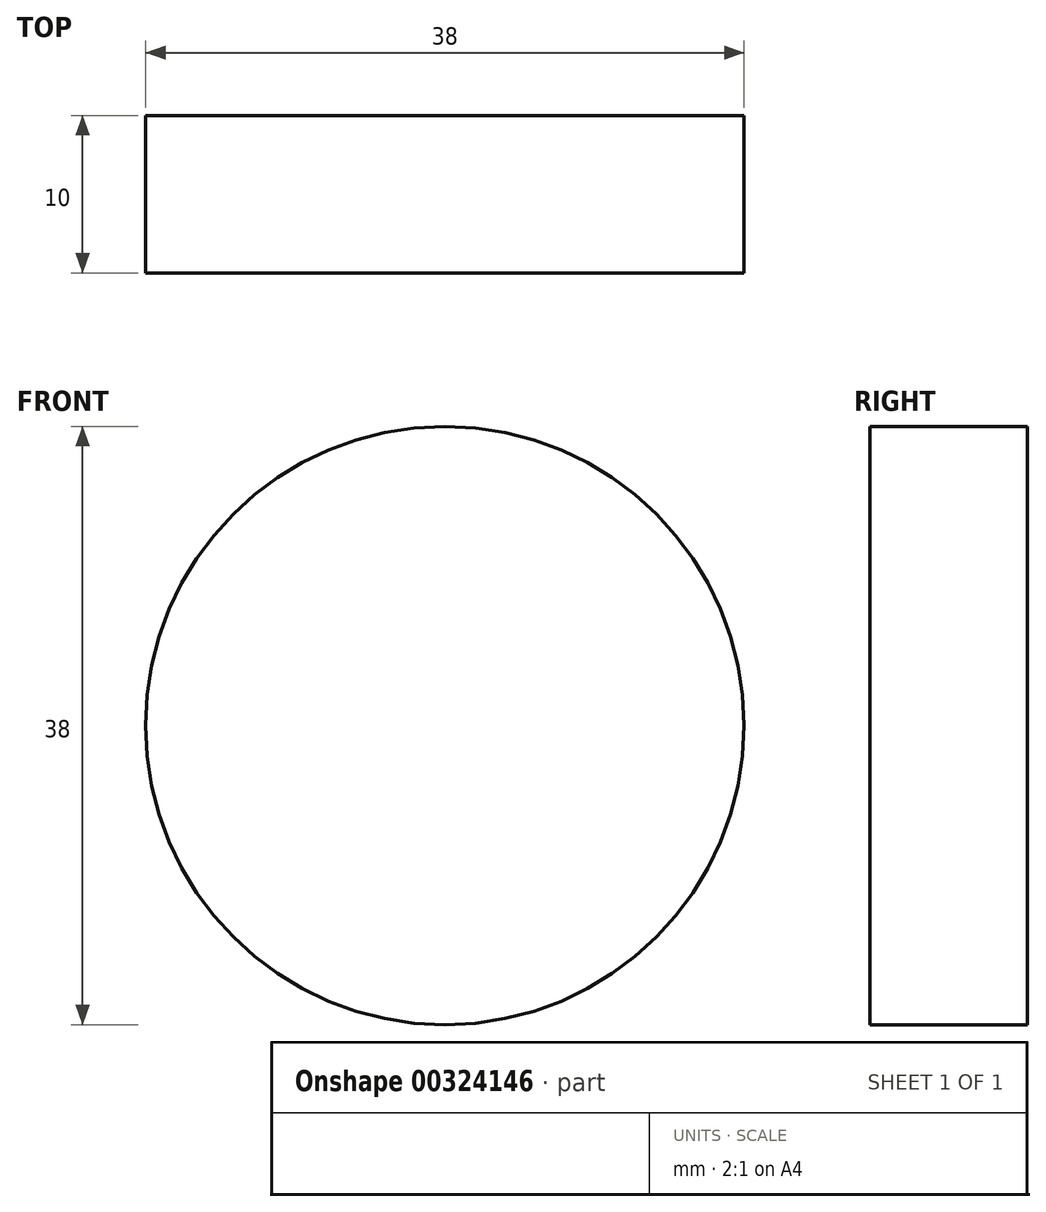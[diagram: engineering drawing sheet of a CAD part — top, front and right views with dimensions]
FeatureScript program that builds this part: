
annotation { "Feature Type Name" : "Feature", "Feature Type Description" : "" }
export const myFeature = defineFeature(function(context is Context, id is Id, definition is map)
    precondition{}
    {
        {
            var Q0;
            Q0=qCreatedBy(makeId("Front.planeOp"),FACE);
            var sketch = newSketch(context, id + "F0", { "sketchPlane" : qUnion([Q0])});
            skCircle(sketch, "E0", {"center": v(0, 0) * mm, "radius": 19 * mm});
            skSolve(sketch);
        }
        {
            var Q0;
            Q0=makeQuery(id+"F0.imprint","IMPRINT",FACE,{"disambiguationData":[TD([[makeQuery(id+"F0.imprint","IMPRINT",EDGE,{"derivedFrom":sQuery(id+"F0.wireOp",EDGE,"E0")}),1.0]])]});
            extrude(context, id + "F1", {"entities" : qUnion([Q0]), "depth" : 10 * mm});
        }
    });
